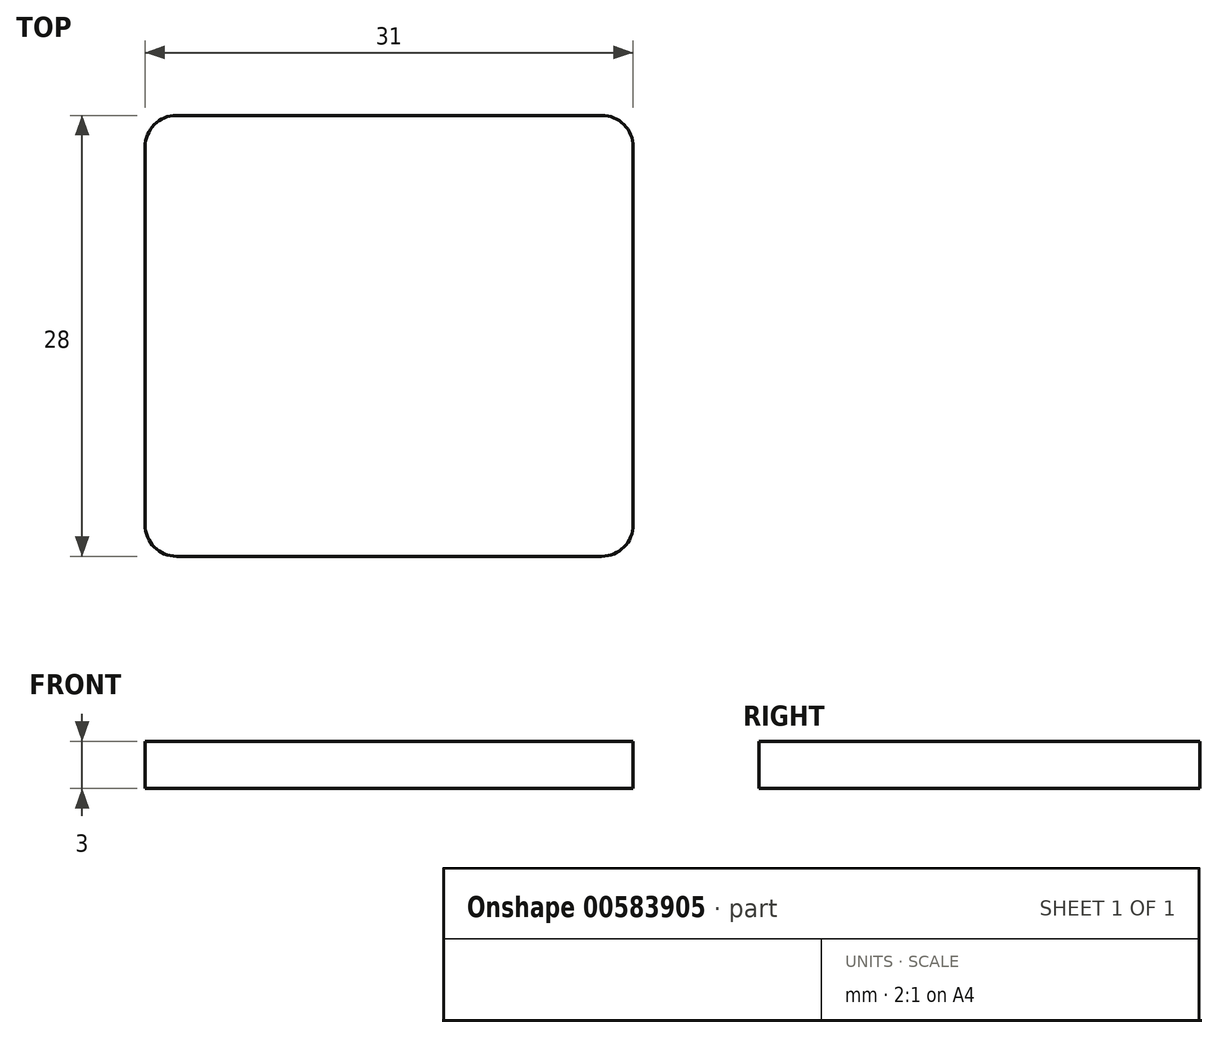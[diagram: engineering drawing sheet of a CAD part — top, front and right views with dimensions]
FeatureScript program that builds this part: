
annotation { "Feature Type Name" : "Feature", "Feature Type Description" : "" }
export const myFeature = defineFeature(function(context is Context, id is Id, definition is map)
    precondition{}
    {
        {
            var Q0;
            Q0=qCreatedBy(makeId("Top.planeOp"),FACE);
            var sketch = newSketch(context, id + "F0", { "sketchPlane" : qUnion([Q0])});
            skLineSegment(sketch, "E0.bottom", {"start": v(12.5, 10.5) * mm, "end": v(-12.5, 10.5) * mm});
            skLineSegment(sketch, "E0.top", {"start": v(12.5, -10.5) * mm, "end": v(-12.5, -10.5) * mm});
            skLineSegment(sketch, "E0.left", {"start": v(12.5, 10.5) * mm, "end": v(12.5, -10.5) * mm});
            skLineSegment(sketch, "E0.right", {"start": v(-12.5, 10.5) * mm, "end": v(-12.5, -10.5) * mm});
            skPoint(sketch, "E0.middle", {"position": v(0, 0) * mm});
            skLineSegment(sketch, "E1.bottom", {"start": v(13.5, 14) * mm, "end": v(-13.5, 14) * mm});
            skLineSegment(sketch, "E1.top", {"start": v(13.5, -14) * mm, "end": v(-13.5, -14) * mm});
            skLineSegment(sketch, "E1.left", {"start": v(15.5, 12) * mm, "end": v(15.5, -12) * mm});
            skLineSegment(sketch, "E1.right", {"start": v(-15.5, 12) * mm, "end": v(-15.5, -12) * mm});
            skLineSegment(sketch, "E2", {"start": v(-12.5, 5.2) * mm, "end": v(12.5, 5.2) * mm, "construction": true});
            skCircle(sketch, "E3", {"center": v(7.5, 5.2) * mm, "radius": 2.65 * mm});
            skCircle(sketch, "E4", {"center": v(-7.5, 5.2) * mm, "radius": 2.65 * mm});
            skCircle(sketch, "E5", {"center": v(-7.5, 5.2) * mm, "radius": 3 * mm});
            skCircle(sketch, "E6", {"center": v(7.5, 5.2) * mm, "radius": 3 * mm});
            skLineSegment(sketch, "E7", {"start": v(7.5, 5.2) * mm, "end": v(7.5, -10.5) * mm, "construction": true});
            skLineSegment(sketch, "E8", {"start": v(-7.5, 5.2) * mm, "end": v(-7.5, -10.5) * mm, "construction": true});
            skLineSegment(sketch, "E9.bottom", {"start": v(9, 0.3) * mm, "end": v(6, 0.3) * mm});
            skLineSegment(sketch, "E9.top", {"start": v(9, -5.7) * mm, "end": v(6, -5.7) * mm});
            skLineSegment(sketch, "E9.left", {"start": v(9, 0.3) * mm, "end": v(9, -5.7) * mm});
            skLineSegment(sketch, "E9.right", {"start": v(6, 0.3) * mm, "end": v(6, -5.7) * mm});
            skPoint(sketch, "E9.middle", {"position": v(7.5, -2.7) * mm});
            skLineSegment(sketch, "E10.bottom", {"start": v(-6, 0.3) * mm, "end": v(-9, 0.3) * mm});
            skLineSegment(sketch, "E10.top", {"start": v(-6, -5.7) * mm, "end": v(-9, -5.7) * mm});
            skLineSegment(sketch, "E10.left", {"start": v(-6, 0.3) * mm, "end": v(-6, -5.7) * mm});
            skLineSegment(sketch, "E10.right", {"start": v(-9, 0.3) * mm, "end": v(-9, -5.7) * mm});
            skPoint(sketch, "E10.middle", {"position": v(-7.5, -2.7) * mm});
            skPoint(sketch, "E11.visualSharp", {"position": v(-15.5, 14) * mm});
            skArc(sketch, "E11.filletArc", {"start": v(-13.5, 14) * mm, "mid": v(-14.91, 13.41) * mm, "end": v(-15.5, 12) * mm});
            skPoint(sketch, "E12.visualSharp", {"position": v(15.5, 14) * mm});
            skArc(sketch, "E12.filletArc", {"start": v(15.5, 12) * mm, "mid": v(14.91, 13.41) * mm, "end": v(13.5, 14) * mm});
            skPoint(sketch, "E13.visualSharp", {"position": v(15.5, -14) * mm});
            skArc(sketch, "E13.filletArc", {"start": v(13.5, -14) * mm, "mid": v(14.91, -13.41) * mm, "end": v(15.5, -12) * mm});
            skPoint(sketch, "E14.visualSharp", {"position": v(-15.5, -14) * mm});
            skArc(sketch, "E14.filletArc", {"start": v(-15.5, -12) * mm, "mid": v(-14.91, -13.41) * mm, "end": v(-13.5, -14) * mm});
            skSolve(sketch);
        }
        {
            var Q0;
            Q0=makeQuery(id+"F0.imprint","IMPRINT",FACE,{"disambiguationData":[TD([[makeQuery(id+"F0.imprint","IMPRINT",EDGE,{"derivedFrom":sQuery(id+"F0.wireOp",EDGE,"E3")}),1.0]])]});
            var Q1;
            Q1=makeQuery(id+"F0.imprint","IMPRINT",FACE,{"disambiguationData":[TD([[makeQuery(id+"F0.imprint","IMPRINT",EDGE,{"derivedFrom":sQuery(id+"F0.wireOp",EDGE,"E4")}),1.0]])]});
            var Q2;
            Q2=makeQuery(id+"F0.imprint","IMPRINT",FACE,{"disambiguationData":[TD([[makeQuery(id+"F0.imprint","IMPRINT",EDGE,{"derivedFrom":sQuery(id+"F0.wireOp",EDGE,"E9.bottom")}),1.0]])]});
            var Q3;
            Q3=makeQuery(id+"F0.imprint","IMPRINT",FACE,{"disambiguationData":[TD([[makeQuery(id+"F0.imprint","IMPRINT",EDGE,{"derivedFrom":sQuery(id+"F0.wireOp",EDGE,"E10.bottom")}),1.0]])]});
            var Q4;
            Q4=makeQuery(id+"F0.imprint","IMPRINT",FACE,{"disambiguationData":[TD([[makeQuery(id+"F0.imprint","IMPRINT",EDGE,{"derivedFrom":sQuery(id+"F0.wireOp",EDGE,"E3")}),-1.0]])]});
            var Q5;
            Q5=makeQuery(id+"F0.imprint","IMPRINT",FACE,{"disambiguationData":[TD([[makeQuery(id+"F0.imprint","IMPRINT",EDGE,{"derivedFrom":sQuery(id+"F0.wireOp",EDGE,"E4")}),-1.0]])]});
            var Q6;
            Q6=makeQuery(id+"F0.imprint","IMPRINT",FACE,{"disambiguationData":[TD([[makeQuery(id+"F0.imprint","IMPRINT",EDGE,{"derivedFrom":sQuery(id+"F0.wireOp",EDGE,"E0.bottom")}),-1.0]])]});
            var Q7;
            Q7=makeQuery(id+"F0.imprint","IMPRINT",FACE,{"disambiguationData":[TD([[makeQuery(id+"F0.imprint","IMPRINT",EDGE,{"derivedFrom":sQuery(id+"F0.wireOp",EDGE,"E0.bottom")}),1.0]])]});
            extrude(context, id + "F1", {"entities" : qUnion([Q0, Q1, Q2, Q3, Q4, Q5, Q6, Q7]), "depth" : 3 * mm, "offsetDistance" : 25 * mm});
        }
    });
